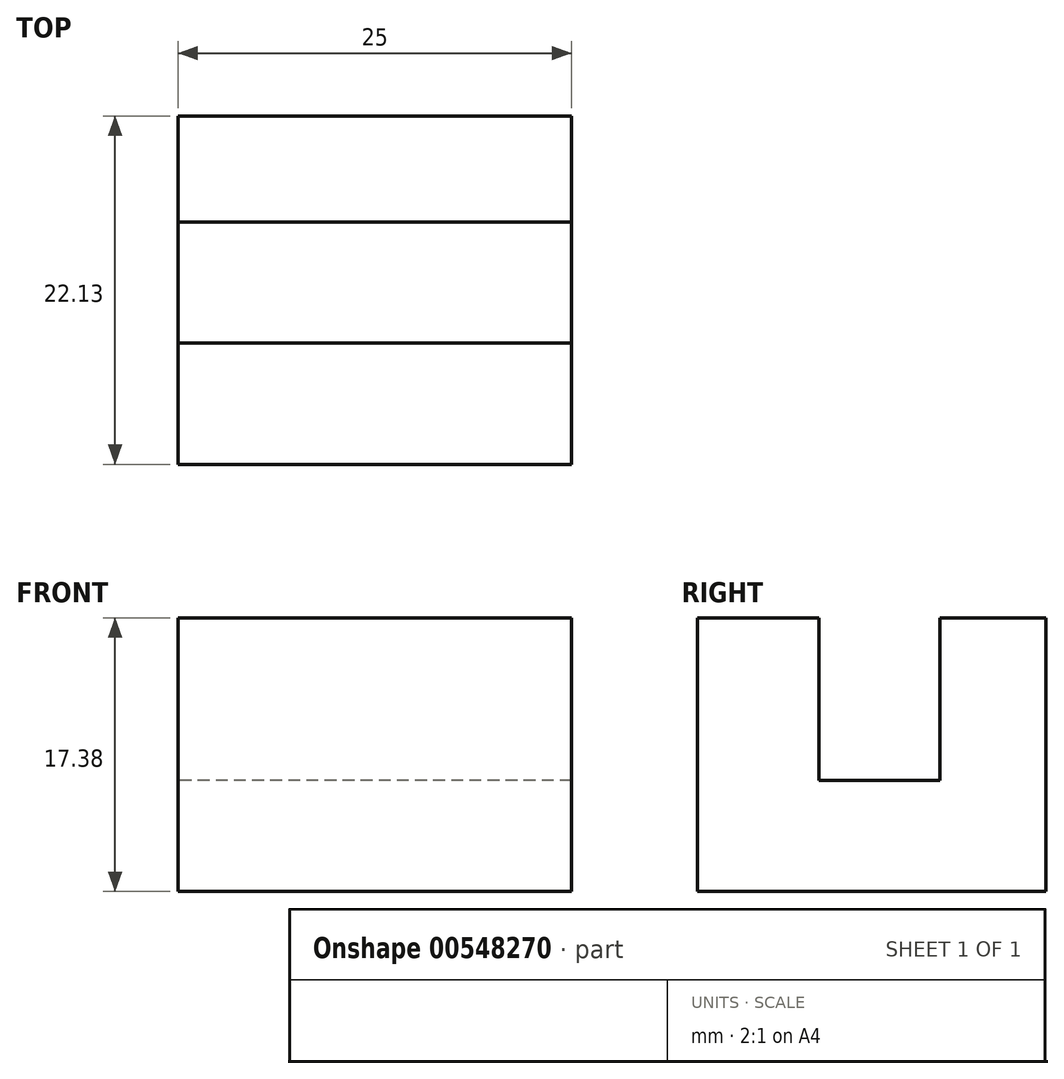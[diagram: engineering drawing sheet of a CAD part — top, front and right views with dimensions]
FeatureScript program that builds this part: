
annotation { "Feature Type Name" : "Feature", "Feature Type Description" : "" }
export const myFeature = defineFeature(function(context is Context, id is Id, definition is map)
    precondition{}
    {
        {
            var Q0;
            Q0=qCreatedBy(makeId("Right.planeOp"),FACE);
            var sketch = newSketch(context, id + "F0", { "sketchPlane" : qUnion([Q0])});
            skLineSegment(sketch, "E0.bottom", {"start": v(21.15, -40.8) * mm, "end": v(-0.98, -40.8) * mm});
            skLineSegment(sketch, "E0.top", {"start": v(21.15, -58.18) * mm, "end": v(-0.98, -58.18) * mm});
            skLineSegment(sketch, "E0.left", {"start": v(21.15, -40.8) * mm, "end": v(21.15, -58.18) * mm});
            skLineSegment(sketch, "E0.right", {"start": v(-0.98, -40.8) * mm, "end": v(-0.98, -58.18) * mm});
            skLineSegment(sketch, "E1.bottom", {"start": v(14.4, -40.8) * mm, "end": v(6.71, -40.8) * mm});
            skLineSegment(sketch, "E1.top", {"start": v(14.4, -51.12) * mm, "end": v(6.71, -51.12) * mm});
            skLineSegment(sketch, "E1.left", {"start": v(14.4, -40.8) * mm, "end": v(14.4, -51.12) * mm});
            skLineSegment(sketch, "E1.right", {"start": v(6.71, -40.8) * mm, "end": v(6.71, -51.12) * mm});
            skSolve(sketch);
        }
        {
            var Q0;
            Q0=makeQuery(id+"F0.imprint","IMPRINT",FACE,{"disambiguationData":[TD([[makeQuery(id+"F0.imprint","IMPRINT",EDGE,{"derivedFrom":sQuery(id+"F0.wireOp",EDGE,"E0.top")}),-1.0]])]});
            extrude(context, id + "F1", {"entities" : qUnion([Q0]), "depth" : 25 * mm});
        }
    });
